# Revit family: FUSE USB (CE)
name_source: partatom
category: Lighting Fixtures
revit_build: Autodesk Revit 2018 (Build: 20170223_1515(x64)
units: mm (PartAtom-declared; Revit-internal decimal feet)

## family parameters
Always vertical = Yes
Cut with Voids When Loaded = No
Host = Wall
Light Source = Yes
OmniClass Number = 23.80.70.00
OmniClass Title = Lighting
Part Type = Normal
Room Calculation Point = No
Round Connector Dimension = Use Diameter
Shared = No

## types (6) — shared parameters
ADA compliant = N / A
Color Filter = 16777215
Dimmable = No
Dimming Lamp Color Temperature Shift = <None>
Driver Included = Yes
Driver Required = No
Efficacy (lm/w) = 39
Electrical Class = 1
Emit from Line Length = 610 mm
Lamp = LED
Light Source Fixed = Yes
Location / IP Rating = IP20
Main Material = Metal - Aluminium / Polycarbonate
Manufacturer = Astro Lighting Ltd
Manufacturer URL - Europe and Rest of World = www.astrolighting.com
Manufacturer URL - North America = us.astrolighting.com
Photometric Web File = 1215081_Fuse LED USB Matt White_Photometry_IES_Iss. 01.ies
Power (Watts) = 3.6
Product CCT = 2700K
Product CRI = 90
Product Dimensions (MM) = 200 x 75 x 92
Product Location = Wall / Headboard
Product Name = Fuse LED USB
Product Weight (KG) = 0.54
Tilt Angle = 60.00°
URL = www.astrolighting.com
Wattage Comments = Not Including USB Load

## per-type parameters (varying)
| type | Main Finish | Product SKU | Product URL |
| Astro Fuse LED USB - Matt White | Matt White | 1215081 | www.astrolighting.com/1215081 |
| Astro Fuse LED USB - Matt Black | Matt Black | 1215082 | www.astrolighting.com/1215082 |
| Astro Fuse LED USB - Polished Chrome | Polished Chrome | 1215083 | www.astrolighting.com/1215083 |
| Astro Fuse LED USB - Matt Nickel | Matt Nickel | 1215084 | www.astrolighting.com/1215084 |
| Astro Fuse LED USB - Bronze | Bronze | 1215085 | www.astrolighting.com/1215085 |
| Astro Fuse LED USB - Matt Gold | Matt Gold | 1215103 | www.astrolighting.com/1215103 |

## geometry (parser evidence)
native form markers: Sweep x2
no freeform markers — native parametric forms only
